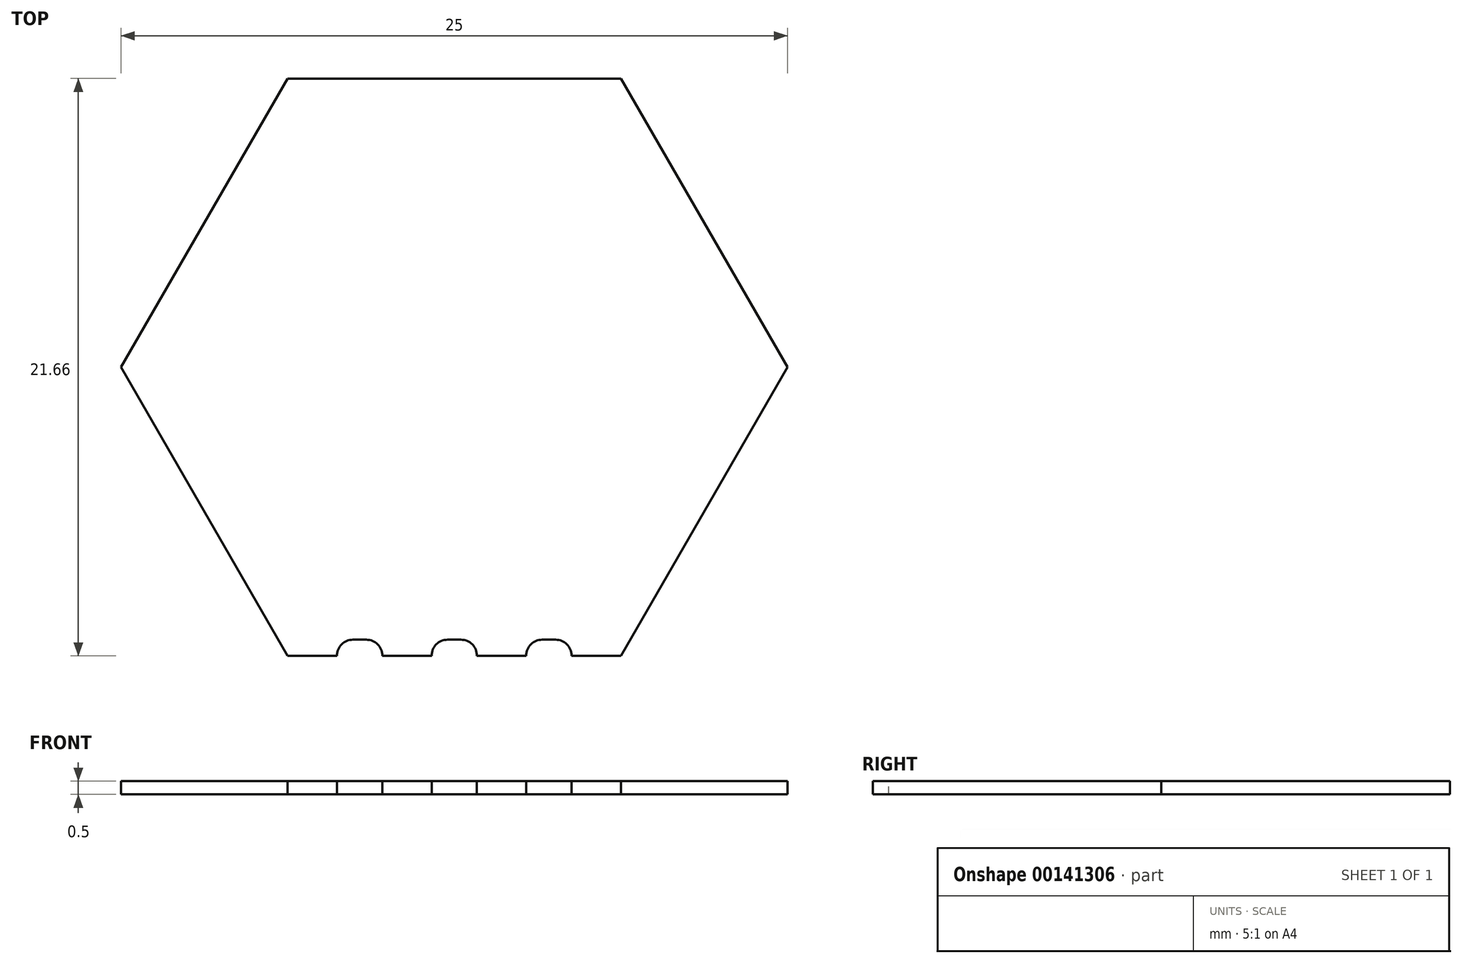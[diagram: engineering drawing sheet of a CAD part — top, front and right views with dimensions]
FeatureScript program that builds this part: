
annotation { "Feature Type Name" : "Feature", "Feature Type Description" : "" }
export const myFeature = defineFeature(function(context is Context, id is Id, definition is map)
    precondition{}
    {
        {
            var Q0;
            Q0=qCreatedBy(makeId("Top.planeOp"),FACE);
            var sketch = newSketch(context, id + "F0", { "sketchPlane" : qUnion([Q0])});
            skCircle(sketch, "E0.cCircle", {"center": v(0, 0) * mm, "radius": 12.5 * mm, "construction": true});
            skLineSegment(sketch, "E0.0", {"start": v(12.5, 0) * mm, "end": v(6.25, -10.83) * mm});
            skLineSegment(sketch, "E0.1", {"start": v(6.25, -10.83) * mm, "end": v(-6.25, -10.83) * mm});
            skLineSegment(sketch, "E0.2", {"start": v(-6.25, -10.83) * mm, "end": v(-12.5, 0) * mm});
            skLineSegment(sketch, "E0.3", {"start": v(-12.5, 0) * mm, "end": v(-6.25, 10.83) * mm});
            skLineSegment(sketch, "E0.4", {"start": v(-6.25, 10.83) * mm, "end": v(6.25, 10.83) * mm});
            skLineSegment(sketch, "E0.5", {"start": v(6.25, 10.83) * mm, "end": v(12.5, 0) * mm});
            skSolve(sketch);
        }
        {
            var Q0;
            Q0=qSketchRegion(id+"F0",true);
            extrude(context, id + "F1", {"entities" : qUnion([Q0]), "depth" : 0.5 * mm});
        }
        {
            var Q0;
            Q0=makeQuery(id+"F1.opExtrude","CAP_FACE",FACE,{"disambiguationData":[OSD([sQuery(id+"F0.wireOp",EDGE,"E0.0"),sQuery(id+"F0.wireOp",EDGE,"E0.1"),sQuery(id+"F0.wireOp",EDGE,"E0.2"),sQuery(id+"F0.wireOp",EDGE,"E0.3"),sQuery(id+"F0.wireOp",EDGE,"E0.4"),sQuery(id+"F0.wireOp",EDGE,"E0.5")])],"isStart":false});
            var sketch = newSketch(context, id + "F2", { "sketchPlane" : qUnion([Q0])});
            skLineSegment(sketch, "E1", {"start": v(3.8, -10.23) * mm, "end": v(3.3, -10.23) * mm});
            skArc(sketch, "E2", {"start": v(3.3, -10.23) * mm, "mid": v(2.88, -10.4) * mm, "end": v(2.7, -10.83) * mm});
            skArc(sketch, "E3", {"start": v(4.4, -10.83) * mm, "mid": v(4.22, -10.4) * mm, "end": v(3.8, -10.23) * mm});
            skLineSegment(sketch, "E4", {"start": v(2.7, -10.83) * mm, "end": v(4.4, -10.83) * mm});
            skPoint(sketch, "E5", {"position": v(-6.25, -10.83) * mm});
            skPoint(sketch, "E6", {"position": v(6.25, -10.83) * mm});
            skLineSegment(sketch, "E7.0", {"start": v(4.4, -10.83) * mm, "end": v(2.7, -10.83) * mm, "construction": true});
            skLineSegment(sketch, "E8", {"start": v(0.25, -10.23) * mm, "end": v(-0.25, -10.23) * mm});
            skArc(sketch, "E9", {"start": v(-0.25, -10.23) * mm, "mid": v(-0.67, -10.4) * mm, "end": v(-0.85, -10.83) * mm});
            skArc(sketch, "E10", {"start": v(0.85, -10.83) * mm, "mid": v(0.67, -10.4) * mm, "end": v(0.25, -10.23) * mm});
            skLineSegment(sketch, "E11", {"start": v(-0.85, -10.83) * mm, "end": v(0.85, -10.83) * mm});
            skLineSegment(sketch, "E12", {"start": v(-3.3, -10.23) * mm, "end": v(-3.8, -10.23) * mm});
            skArc(sketch, "E13", {"start": v(-3.8, -10.23) * mm, "mid": v(-4.22, -10.4) * mm, "end": v(-4.4, -10.83) * mm});
            skArc(sketch, "E14", {"start": v(-2.7, -10.83) * mm, "mid": v(-2.88, -10.4) * mm, "end": v(-3.3, -10.23) * mm});
            skLineSegment(sketch, "E15", {"start": v(-4.4, -10.83) * mm, "end": v(-2.7, -10.83) * mm});
            skLineSegment(sketch, "E16.trimOffspring", {"start": v(0.85, -10.83) * mm, "end": v(-6.25, -10.83) * mm, "construction": true});
            skLineSegment(sketch, "E17", {"start": v(0.85, -10.83) * mm, "end": v(2.7, -10.83) * mm, "construction": true});
            skLineSegment(sketch, "E18", {"start": v(4.4, -10.83) * mm, "end": v(6.25, -10.83) * mm, "construction": true});
            skSolve(sketch);
        }
        {
            var Q0;
            Q0=qSketchRegion(id+"F2",true);
            extrude(context, id + "F3", {"entities" : qUnion([Q0]), "operationType" : NewBodyOperationType.REMOVE, "endBound" : BoundingType.THROUGH_ALL, "oppositeDirection" : true, "depth" : 25 * mm});
        }
    });
